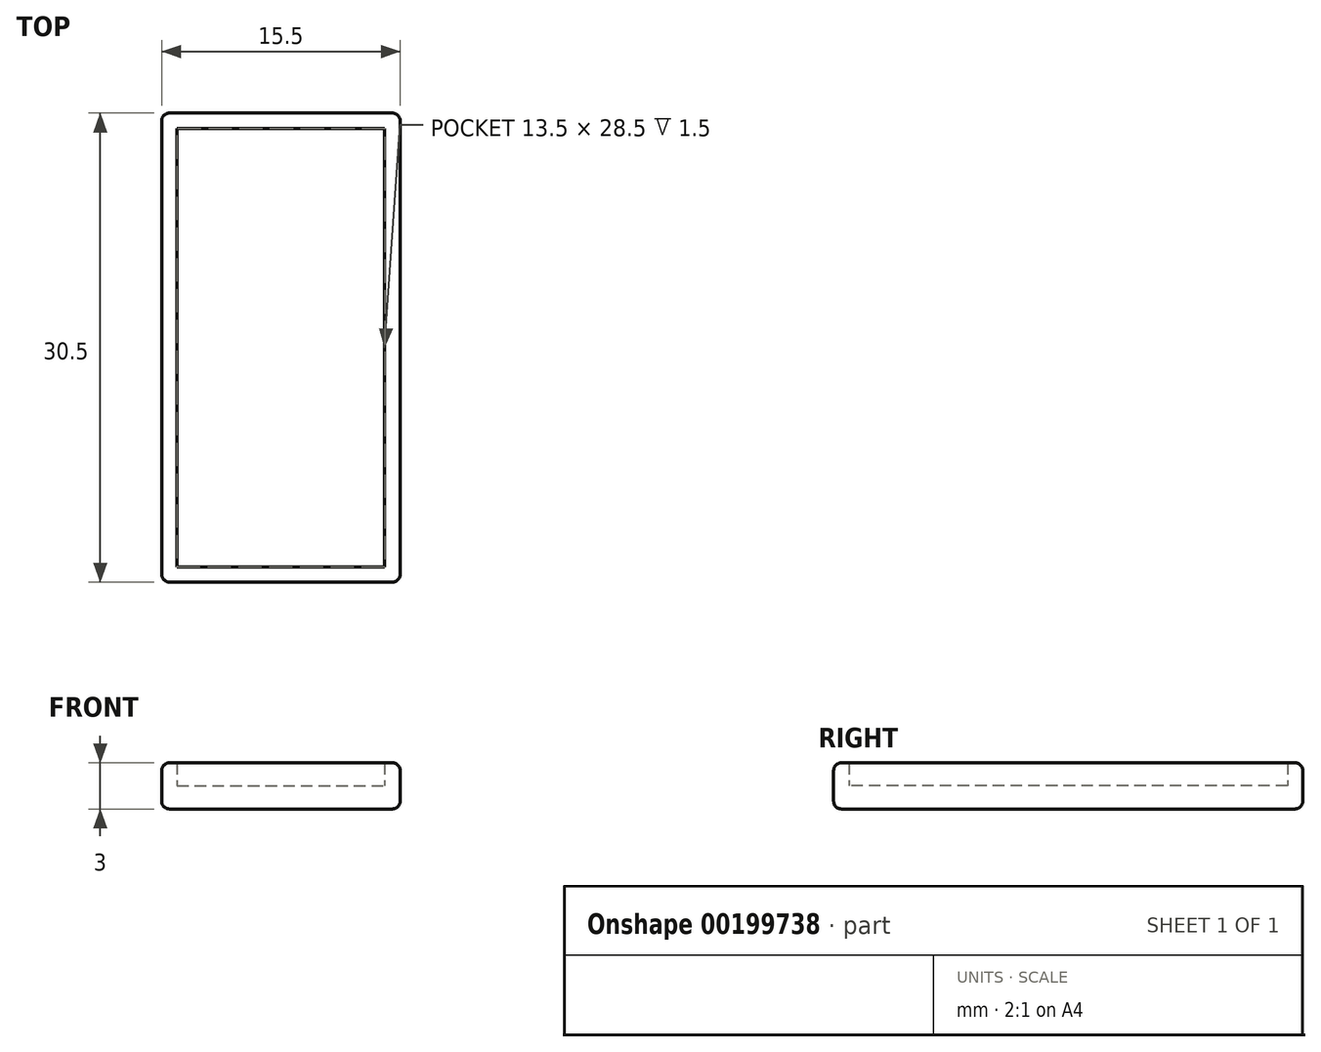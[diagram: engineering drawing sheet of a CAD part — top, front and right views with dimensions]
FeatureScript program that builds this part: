
annotation { "Feature Type Name" : "Feature", "Feature Type Description" : "" }
export const myFeature = defineFeature(function(context is Context, id is Id, definition is map)
    precondition{}
    {
        {
            var Q0;
            Q0=qCreatedBy(makeId("Top.planeOp"),FACE);
            var sketch = newSketch(context, id + "F0", { "sketchPlane" : qUnion([Q0])});
            skLineSegment(sketch, "E0.bottom", {"start": v(-8.41, 17.06) * mm, "end": v(5.09, 17.06) * mm});
            skLineSegment(sketch, "E0.top", {"start": v(-8.41, -11.44) * mm, "end": v(5.09, -11.44) * mm});
            skLineSegment(sketch, "E0.left", {"start": v(-8.41, 17.06) * mm, "end": v(-8.41, -11.44) * mm});
            skLineSegment(sketch, "E0.right", {"start": v(5.09, 17.06) * mm, "end": v(5.09, -11.44) * mm});
            skLineSegment(sketch, "E1.bottom", {"start": v(-9.41, 18.06) * mm, "end": v(6.09, 18.06) * mm});
            skLineSegment(sketch, "E1.top", {"start": v(-9.41, -12.44) * mm, "end": v(6.09, -12.44) * mm});
            skLineSegment(sketch, "E1.left", {"start": v(-9.41, 18.06) * mm, "end": v(-9.41, -12.44) * mm});
            skLineSegment(sketch, "E1.right", {"start": v(6.09, 18.06) * mm, "end": v(6.09, -12.44) * mm});
            skSolve(sketch);
        }
        {
            var Q0;
            Q0=makeQuery(id+"F0.imprint","IMPRINT",FACE,{"disambiguationData":[TD([[makeQuery(id+"F0.imprint","IMPRINT",EDGE,{"derivedFrom":sQuery(id+"F0.wireOp",EDGE,"E0.bottom")}),1.0]])]});
            extrude(context, id + "F1", {"entities" : qUnion([Q0]), "depth" : 3 * mm});
        }
        {
            var Q0;
            Q0=makeQuery(id+"F0.imprint","IMPRINT",FACE,{"disambiguationData":[TD([[makeQuery(id+"F0.imprint","IMPRINT",EDGE,{"derivedFrom":sQuery(id+"F0.wireOp",EDGE,"E0.bottom")}),-1.0]])]});
            extrude(context, id + "F2", {"entities" : qUnion([Q0]), "operationType" : NewBodyOperationType.ADD, "depth" : 1.5 * mm});
        }
        {
            var Q0;
            Q0=makeQuery(id+"F1.opExtrude","SWEPT_FACE",FACE,{"disambiguationData":[OSD([sQuery(id+"F0.wireOp",EDGE,"E1.right")])]});
            var Q1;
            Q1=makeQuery(id+"F1.opExtrude","SWEPT_FACE",FACE,{"disambiguationData":[OSD([sQuery(id+"F0.wireOp",EDGE,"E1.top")])]});
            var Q2;
            Q2=makeQuery(id+"F1.opExtrude","SWEPT_FACE",FACE,{"disambiguationData":[OSD([sQuery(id+"F0.wireOp",EDGE,"E1.left")])]});
            var Q3;
            Q3=makeQuery(id+"F1.opExtrude","SWEPT_FACE",FACE,{"disambiguationData":[OSD([sQuery(id+"F0.wireOp",EDGE,"E1.bottom")])]});
            fillet(context, id + "F3", {"entities" : qUnion([Q0, Q1, Q2, Q3]), "radius" : 0.5 * mm, "tangentPropagation" : true, "allowEdgeOverflow" : false});
        }
    });
